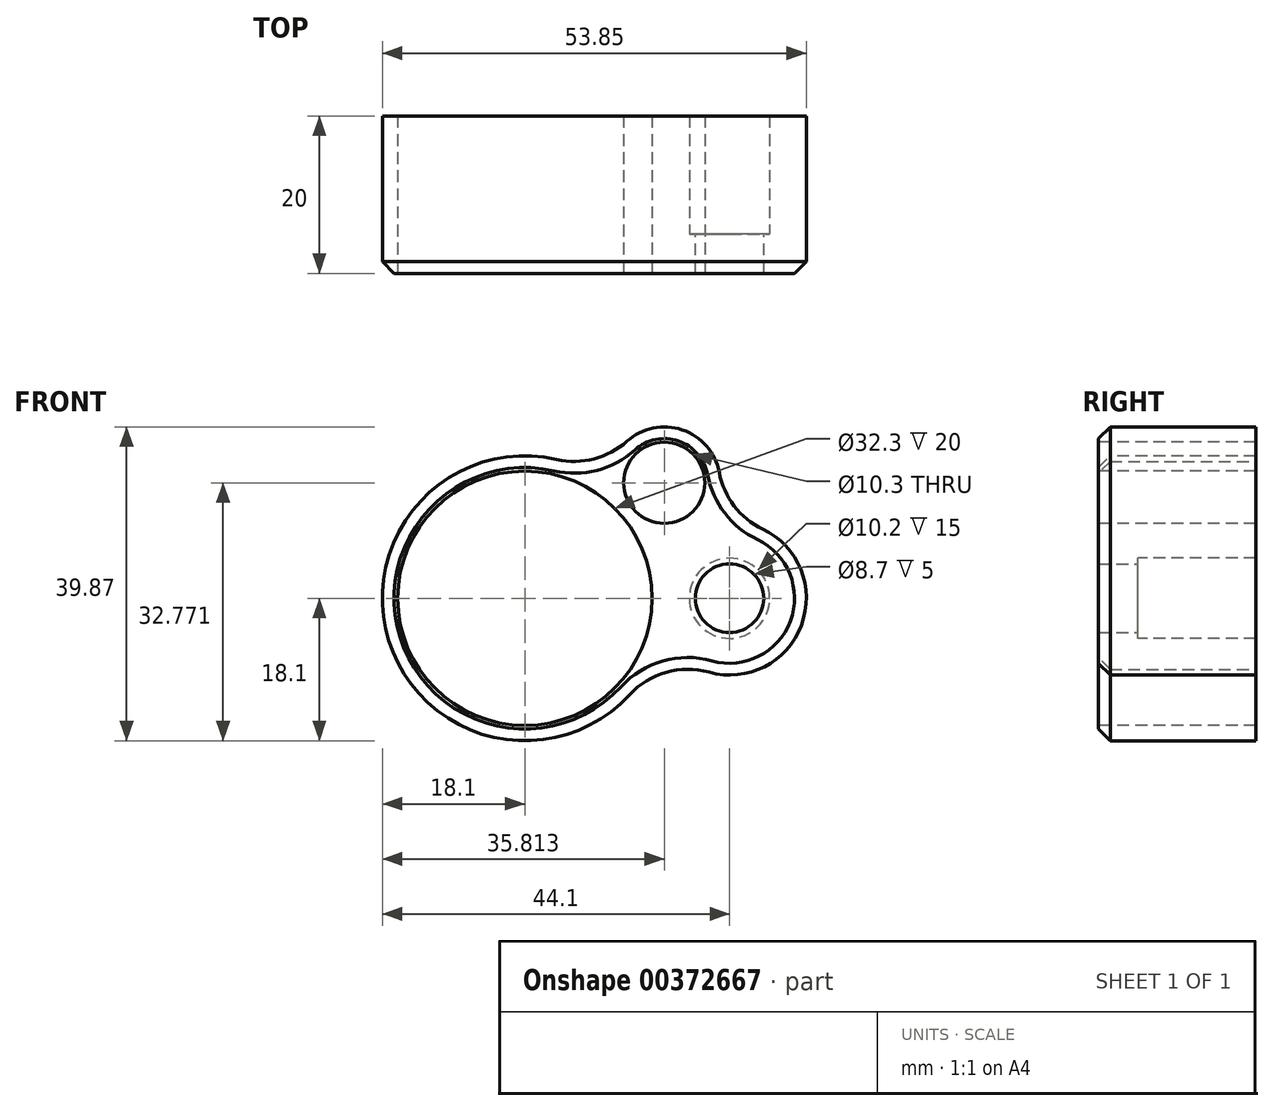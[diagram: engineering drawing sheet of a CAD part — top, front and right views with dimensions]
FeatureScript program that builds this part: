
annotation { "Feature Type Name" : "Feature", "Feature Type Description" : "" }
export const myFeature = defineFeature(function(context is Context, id is Id, definition is map)
    precondition{}
    {
        {
            var Q0;
            Q0=qCreatedBy(makeId("Front.planeOp"),FACE);
            var sketch = newSketch(context, id + "F0", { "sketchPlane" : qUnion([Q0])});
            skCircle(sketch, "E0", {"center": v(0, 0) * mm, "radius": 16.15 * mm});
            skArc(sketch, "E1", {"start": v(21.2, 8.49) * mm, "mid": v(21.29, 20.8) * mm, "end": v(10.61, 14.66) * mm});
            skArc(sketch, "E2", {"start": v(10.61, 14.66) * mm, "mid": v(-17.06, -6.04) * mm, "end": v(17.47, -4.73) * mm});
            skCircle(sketch, "E3.converted", {"center": v(17.71, 14.67) * mm, "radius": 5.15 * mm});
            skCircle(sketch, "E4", {"center": v(26, 0) * mm, "radius": 4.35 * mm});
            skArc(sketch, "E5", {"start": v(17.47, -4.73) * mm, "mid": v(35.38, -2.65) * mm, "end": v(21.2, 8.49) * mm});
            skLineSegment(sketch, "E6", {"start": v(0, 0) * mm, "end": v(19.71, 11.13) * mm, "construction": true});
            skLineSegment(sketch, "E7", {"start": v(17.71, 14.67) * mm, "end": v(26, 0) * mm, "construction": true});
            skCircle(sketch, "E8", {"center": v(26, 0) * mm, "radius": 5.1 * mm});
            skSolve(sketch);
        }
        {
            var Q0;
            Q0=makeQuery(id+"F0.imprint","IMPRINT",FACE,{"disambiguationData":[TD([[makeQuery(id+"F0.imprint","IMPRINT",EDGE,{"derivedFrom":sQuery(id+"F0.wireOp",EDGE,"E0")}),-1.0]])]});
            var Q1;
            {var subQ0=sQuery(id+"F0.wireOp",EDGE,"E5");var subQ1=sQuery(id+"F0.wireOp",EDGE,"E1");var subQ2=makeQuery(id+"F0.imprint","INTERSECT",VERTEX,{"derivedFrom":[subQ1,subQ0]});Q1=makeQuery(id+"F0.imprint","IMPRINT",FACE,{"disambiguationData":[TD([[makeQuery(id+"F0.imprint","IMPRINT",EDGE,{"disambiguationData":[TD([[subQ2,-1.0]])],"derivedFrom":subQ1}),1.0]])]});}
            extrude(context, id + "F1", {"entities" : qUnion([Q0, Q1]), "oppositeDirection" : true, "depth" : 15 * mm, "offsetDistance" : 25 * mm});
        }
        {
            var Q0;
            Q0=makeQuery(id+"F0.imprint","IMPRINT",FACE,{"disambiguationData":[TD([[makeQuery(id+"F0.imprint","IMPRINT",EDGE,{"derivedFrom":sQuery(id+"F0.wireOp",EDGE,"E0")}),-1.0]])]});
            var Q1;
            Q1=makeQuery(id+"F0.imprint","IMPRINT",FACE,{"disambiguationData":[TD([[makeQuery(id+"F0.imprint","IMPRINT",EDGE,{"derivedFrom":sQuery(id+"F0.wireOp",EDGE,"E4")}),-1.0]])]});
            extrude(context, id + "F2", {"entities" : qUnion([Q0, Q1]), "operationType" : NewBodyOperationType.ADD, "depth" : 5 * mm, "offsetDistance" : 25 * mm});
        }
        {
            var Q0;
            Q0=makeQuery(id+"F1.opExtrude","SWEPT_EDGE",EDGE,{"disambiguationData":[OSD([sQuery(id+"F0.wireOp",EDGE,"E1"),sQuery(id+"F0.wireOp",EDGE,"E2")])]});
            var Q1;
            Q1=makeQuery(id+"F1.opExtrude","SWEPT_EDGE",EDGE,{"disambiguationData":[OSD([sQuery(id+"F0.wireOp",EDGE,"E1"),sQuery(id+"F0.wireOp",EDGE,"E5")])]});
            var Q2;
            Q2=makeQuery(id+"F1.opExtrude","SWEPT_EDGE",EDGE,{"disambiguationData":[OSD([sQuery(id+"F0.wireOp",EDGE,"E2"),sQuery(id+"F0.wireOp",EDGE,"E5")])]});
            fillet(context, id + "F3", {"entities" : qUnion([Q0, Q1, Q2]), "radius" : 10 * mm, "tangentPropagation" : true, "allowEdgeOverflow" : false});
        }
        {
            var Q0;
            Q0=makeQuery(id+"F2.opExtrude","CAP_EDGE",EDGE,{"disambiguationData":[OSD([sQuery(id+"F0.wireOp",EDGE,"E2")])],"isStart":false});
            chamfer(context, id + "F4", {"entities" : qUnion([Q0]), "width" : 1.5 * mm, "tangentPropagation" : true});
        }
    });
